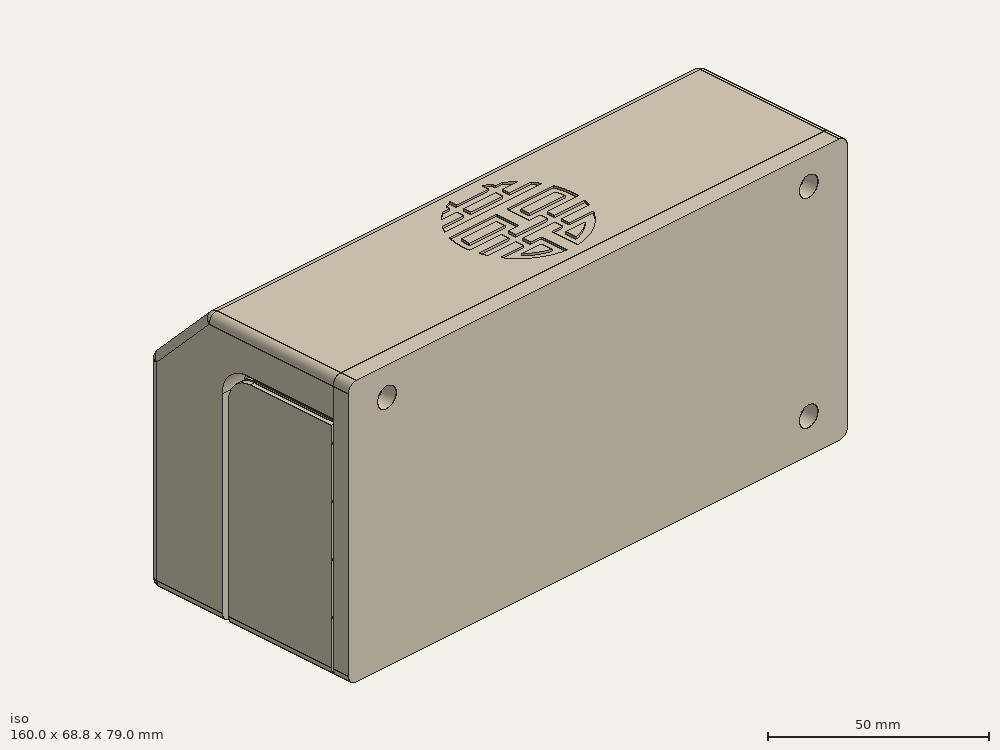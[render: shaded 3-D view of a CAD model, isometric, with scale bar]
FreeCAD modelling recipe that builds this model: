
FCSTD DOCUMENT  (FreeCAD 1.0R39109 (Git))
Label: plastic-player-3
License: All rights reserved
LicenseURL: https://en.wikipedia.org/wiki/All_rights_reserved
objects: Part::Feature×120, Part::Box×46, Part::Mirroring×22, Part::Cylinder×20, Part::MultiFuse×17, Part::Cut×15, App::Part×11, Part::Fillet×11, Part::Chamfer×9, Part::Extrusion×5, Part::Part2DObjectPython×4, Part::FeaturePython×2, Mesh::Feature×2, Sketcher::SketchObject×1
note: 272 computed .brp shape members not serialized (recipe doc carries the construction recipe); baked Part::Feature solids carry a one-line shape summary decoded from their .brp

FEATURE [Part::Box] Box002  label="Cube002"
  AttacherType = Attacher::AttachEngine3D
  Height = 66
  Length = 7
  Placement = pos=(-80,-24.1,-37.5) rot=(0,0,1;0rad)
  Width = 33.6
FEATURE [Part::Cylinder] Cylinder
  Angle = 360
  AttacherType = Attacher::AttachEngine3D
  FirstAngle = 0
  Height = 10
  Placement = pos=(-55,25.5,-3) rot=(-1,0,0;1.5708rad)
  Radius = 12
  SecondAngle = 0
FEATURE [Part::Mirroring] Part__Mirroring001  label="Cylinder (Mirror #2)"
  Base = (0,0,0)
  Normal = (1,0,0)
  Source = -> Cylinder
FEATURE [Part::Cylinder] Cylinder001
  Angle = 360
  AttacherType = Attacher::AttachEngine3D
  FirstAngle = 0
  Height = 10
  Placement = pos=(0,25.5,-15.7) rot=(-1,0,0;1.5708rad)
  Radius = 2.5
  SecondAngle = 0
FEATURE [Part::Box] Box004  label="SlideHolder"
  AttacherType = Attacher::AttachEngine3D
  Height = 25
  Length = 64
  Placement = pos=(-32,34.3405,-9.84497) rot=(1,0,0;0.872665rad)
  Width = 9
FEATURE [Part::Box] Box005  label="Slit"
  AttacherType = Attacher::AttachEngine3D
  Height = 25
  Length = 63
  Placement = pos=(-31.5,39.3167,-9.43399) rot=(1,0,0;0.872665rad)
  Width = 4
FEATURE [Part::Box] Box006  label="Cube003"
  AttacherType = Attacher::AttachEngine3D
  Height = 60
  Length = 150
  Placement = pos=(-75,35,-37.5) rot=(0,0,1;0rad)
  Width = 50
FEATURE [Part::Cylinder] Cylinder002
  Angle = 360
  AttacherType = Attacher::AttachEngine3D
  FirstAngle = 0
  Height = 10
  Placement = pos=(13.9,22.5265,-9.10218) rot=(-1,0,0;0.698132rad)
  Radius = 1.35
  SecondAngle = 0
FEATURE [Part::Cut] Cut003  label="SlideHolderWithScrewHole"
  Base = -> Box004
  Tool = -> Cylinder002
FEATURE [Part::Cut] Cut002  label="SlideHolderCut"
  Base = -> Cut003
  Tool = -> Box006
FEATURE [Part::Box] Box009  label="Window"
  AttacherType = Attacher::AttachEngine3D
  Height = 12.8
  Length = 23.5
  Placement = pos=(-11.8,23.3449,20.5797) rot=(1,0,0;0.785398rad)
  Width = 20
FEATURE [Part::Cylinder] Cylinder005
  Angle = 360
  AttacherType = Attacher::AttachEngine3D
  FirstAngle = 0
  Height = 10
  Placement = pos=(-23.4,25.8452,-12.1479) rot=(-1,0,0;0.698132rad)
  Radius = 1.35
  SecondAngle = 0
FEATURE [Part::Cut] Cut010  label="SlideHolderWithScrewHoles"
  Base = -> Cut002
  Tool = -> Cylinder005
FEATURE [Part::Box] Box010  label="WindowEthernet"
  AttacherType = Attacher::AttachEngine3D
  Height = 16.9
  Length = 10
  Placement = pos=(-81.7,-17.4,3) rot=(0,0,1;0rad)
  Width = 14.7
FEATURE [Part::Box] Box011  label="WindowUSB3"
  AttacherType = Attacher::AttachEngine3D
  Height = 15
  Length = 10
  Placement = pos=(-81.7,-16.6,-14.6) rot=(0,0,1;0rad)
  Width = 15.4
FEATURE [Part::Box] Box012  label="WindowUSB2"
  AttacherType = Attacher::AttachEngine3D
  Height = 15
  Length = 10
  Placement = pos=(-81.7,-16.6,-32.6) rot=(0,0,1;0rad)
  Width = 15.4
FEATURE [Part::Box] Box013  label="Cube006"
  AttacherType = Attacher::AttachEngine3D
  Height = 10
  Length = 12
  Placement = pos=(-6.6,-18.3,-45.9) rot=(0,0,1;0rad)
  Width = 6.2
FEATURE [Part::Cylinder] Cylinder006  label="WindowJackLarge"
  Angle = 360
  AttacherType = Attacher::AttachEngine3D
  FirstAngle = 0
  Height = 10
  Placement = pos=(-43.3,-13.8,-45.8) rot=(0,0,1;0rad)
  Radius = 5
  SecondAngle = 0
FEATURE [Part::Box] Box014  label="Cube007"
  AttacherType = Attacher::AttachEngine3D
  Height = 10
  Length = 27
  Placement = pos=(-35.7,-20.3,-45.9) rot=(0,0,1;0rad)
  Width = 10.5
FEATURE [Part::Box] Box018  label="Cube008"
  AttacherType = Attacher::AttachEngine3D
  Height = 3
  Length = 10
  Placement = pos=(-35.6,27.9576,-4.6521) rot=(-1,0,0;0.698132rad)
  Width = 5
FEATURE [Part::Cut] Cut019  label="SlideHolderWithInsets"
  Base = -> Cut010
  Tool = -> Box018
FEATURE [Part::Box] Box019  label="WindowHDMI1"
  AttacherType = Attacher::AttachEngine3D
  Height = 10
  Length = 9
  Placement = pos=(-19.7,-17.3,-42) rot=(0,0,1;0rad)
  Width = 5
FEATURE [Part::Box] Box020  label="WindowHDMI2"
  AttacherType = Attacher::AttachEngine3D
  Height = 10
  Length = 9
  Placement = pos=(-33.7,-17.3,-42) rot=(0,0,1;0rad)
  Width = 5
FEATURE [Part::Feature] Part__Feature071  label="PCB, RPi4ModelB"
  shape: bbox 85 x 1.6 x 56 mm, 136 faces (baked)
FEATURE [Part::Feature] Part__Feature072  label="Broadcom BCM2711B0 CPU, RPi4ModelB"
  Placement = pos=(-13.25,0.8,-4.5) rot=(0,0,1;0rad)
  shape: bbox 15 x 0.5 x 15 mm, 10 faces (baked)
FEATURE [Part::Feature] Part__Feature073  label="Broadcom BCM2711B0 CPU, RPi4ModelB001"
  Placement = pos=(-13.25,0.8,-4.5) rot=(0,0,1;0rad)
  shape: bbox 14.6 x 1.8 x 14.6 mm, 19 faces (baked)
FEATURE [App::Part] Broadcom_BCM2711B0_CPU__RPi4ModelB  label="Broadcom BCM2711B0 CPU, RPi4ModelB002"
  Group = -> [Part__Feature072,Part__Feature073]
  Origin = -> Origin021
FEATURE [Part::Feature] Part__Feature074  label="2.54 mm DUPONT MALE PIN HEADER, POE, 2X2, RPi4ModelB"
  Placement = pos=(19,0.8,-18.36) rot=(0,0,1;0rad)
  shape: bbox 5.08 x 2.5 x 5.08 mm, 46 faces (baked)
FEATURE [Part::Feature] Part__Feature075  label="2.54 mm DUPONT MALE PIN HEADER, POE, 2X2, RPi4ModelB001"
  Placement = pos=(19,0.8,-18.36) rot=(0,0,1;0rad)
  shape: bbox 0.64 x 11.3 x 0.64 mm, 14 faces (baked)
FEATURE [Part::Feature] Part__Feature076  label="2.54 mm DUPONT MALE PIN HEADER, POE, 2X2, RPi4ModelB002"
  Placement = pos=(19,0.8,-18.36) rot=(0,0,1;0rad)
  shape: bbox 0.64 x 11.3 x 0.64 mm, 14 faces (baked)
FEATURE [Part::Feature] Part__Feature077  label="2.54 mm DUPONT MALE PIN HEADER, POE, 2X2, RPi4ModelB003"
  Placement = pos=(19,0.8,-18.36) rot=(0,0,1;0rad)
  shape: bbox 0.64 x 11.3 x 0.64 mm, 14 faces (baked)
FEATURE [Part::Feature] Part__Feature078  label="2.54 mm DUPONT MALE PIN HEADER, POE, 2X2, RPi4ModelB004"
  Placement = pos=(19,0.8,-18.36) rot=(0,0,1;0rad)
  shape: bbox 0.64 x 11.3 x 0.64 mm, 14 faces (baked)
FEATURE [App::Part] __54_mm_DUPONT_MALE_PIN_HEADER__POE__2X2__RPi4ModelB  label="2.54 mm DUPONT MALE PIN HEADER, POE, 2X2, RPi4ModelB005"
  Group = -> [Part__Feature074,Part__Feature075,Part__Feature076,Part__Feature077,Part__Feature078]
  Origin = -> Origin022
FEATURE [Part::Feature] Part__Feature079  label="2.54 mm DUPONT MALE PIN HEADER, IO, 2X20, RPi4ModelB"
  Placement = pos=(-10,0.8,-24.5) rot=(0,0,1;0rad)
  shape: bbox 50.8 x 2.5 x 5.08 mm, 298 faces (baked)
FEATURE [Part::Feature] Part__Feature080  label="2.54 mm DUPONT MALE PIN HEADER, IO, 2X20, RPi4ModelB001"
  Placement = pos=(-10,0.8,-24.5) rot=(0,0,1;0rad)
  shape: bbox 0.64 x 11.3 x 0.64 mm, 14 faces (baked)
FEATURE [Part::Feature] Part__Feature081  label="2.54 mm DUPONT MALE PIN HEADER, IO, 2X20, RPi4ModelB002"
  Placement = pos=(-10,0.8,-24.5) rot=(0,0,1;0rad)
  shape: bbox 0.64 x 11.3 x 0.64 mm, 14 faces (baked)
FEATURE [Part::Feature] Part__Feature082  label="2.54 mm DUPONT MALE PIN HEADER, IO, 2X20, RPi4ModelB003"
  Placement = pos=(-10,0.8,-24.5) rot=(0,0,1;0rad)
  shape: bbox 0.64 x 11.3 x 0.64 mm, 14 faces (baked)
FEATURE [Part::Feature] Part__Feature083  label="2.54 mm DUPONT MALE PIN HEADER, IO, 2X20, RPi4ModelB004"
  Placement = pos=(-10,0.8,-24.5) rot=(0,0,1;0rad)
  shape: bbox 0.64 x 11.3 x 0.64 mm, 14 faces (baked)
FEATURE [Part::Feature] Part__Feature084  label="2.54 mm DUPONT MALE PIN HEADER, IO, 2X20, RPi4ModelB005"
  Placement = pos=(-10,0.8,-24.5) rot=(0,0,1;0rad)
  shape: bbox 0.64 x 11.3 x 0.64 mm, 14 faces (baked)
FEATURE [Part::Feature] Part__Feature085  label="2.54 mm DUPONT MALE PIN HEADER, IO, 2X20, RPi4ModelB006"
  Placement = pos=(-10,0.8,-24.5) rot=(0,0,1;0rad)
  shape: bbox 0.64 x 11.3 x 0.64 mm, 14 faces (baked)
FEATURE [Part::Feature] Part__Feature086  label="2.54 mm DUPONT MALE PIN HEADER, IO, 2X20, RPi4ModelB007"
  Placement = pos=(-10,0.8,-24.5) rot=(0,0,1;0rad)
  shape: bbox 0.64 x 11.3 x 0.64 mm, 14 faces (baked)
FEATURE [Part::Feature] Part__Feature087  label="2.54 mm DUPONT MALE PIN HEADER, IO, 2X20, RPi4ModelB008"
  Placement = pos=(-10,0.8,-24.5) rot=(0,0,1;0rad)
  shape: bbox 0.64 x 11.3 x 0.64 mm, 14 faces (baked)
FEATURE [Part::Feature] Part__Feature088  label="2.54 mm DUPONT MALE PIN HEADER, IO, 2X20, RPi4ModelB009"
  Placement = pos=(-10,0.8,-24.5) rot=(0,0,1;0rad)
  shape: bbox 0.64 x 11.3 x 0.64 mm, 14 faces (baked)
FEATURE [Part::Feature] Part__Feature089  label="2.54 mm DUPONT MALE PIN HEADER, IO, 2X20, RPi4ModelB010"
  Placement = pos=(-10,0.8,-24.5) rot=(0,0,1;0rad)
  shape: bbox 0.64 x 11.3 x 0.64 mm, 14 faces (baked)
FEATURE [Part::Feature] Part__Feature090  label="2.54 mm DUPONT MALE PIN HEADER, IO, 2X20, RPi4ModelB011"
  Placement = pos=(-10,0.8,-24.5) rot=(0,0,1;0rad)
  shape: bbox 0.64 x 11.3 x 0.64 mm, 14 faces (baked)
FEATURE [Part::Feature] Part__Feature091  label="2.54 mm DUPONT MALE PIN HEADER, IO, 2X20, RPi4ModelB012"
  Placement = pos=(-10,0.8,-24.5) rot=(0,0,1;0rad)
  shape: bbox 0.64 x 11.3 x 0.64 mm, 14 faces (baked)
FEATURE [Part::Feature] Part__Feature092  label="2.54 mm DUPONT MALE PIN HEADER, IO, 2X20, RPi4ModelB013"
  Placement = pos=(-10,0.8,-24.5) rot=(0,0,1;0rad)
  shape: bbox 0.64 x 11.3 x 0.64 mm, 14 faces (baked)
FEATURE [Part::Feature] Part__Feature093  label="2.54 mm DUPONT MALE PIN HEADER, IO, 2X20, RPi4ModelB014"
  Placement = pos=(-10,0.8,-24.5) rot=(0,0,1;0rad)
  shape: bbox 0.64 x 11.3 x 0.64 mm, 14 faces (baked)
FEATURE [Part::Feature] Part__Feature094  label="2.54 mm DUPONT MALE PIN HEADER, IO, 2X20, RPi4ModelB015"
  Placement = pos=(-10,0.8,-24.5) rot=(0,0,1;0rad)
  shape: bbox 0.64 x 11.3 x 0.64 mm, 14 faces (baked)
FEATURE [Part::Feature] Part__Feature095  label="2.54 mm DUPONT MALE PIN HEADER, IO, 2X20, RPi4ModelB016"
  Placement = pos=(-10,0.8,-24.5) rot=(0,0,1;0rad)
  shape: bbox 0.64 x 11.3 x 0.64 mm, 14 faces (baked)
FEATURE [Part::Feature] Part__Feature096  label="2.54 mm DUPONT MALE PIN HEADER, IO, 2X20, RPi4ModelB017"
  Placement = pos=(-10,0.8,-24.5) rot=(0,0,1;0rad)
  shape: bbox 0.64 x 11.3 x 0.64 mm, 14 faces (baked)
FEATURE [Part::Feature] Part__Feature097  label="2.54 mm DUPONT MALE PIN HEADER, IO, 2X20, RPi4ModelB018"
  Placement = pos=(-10,0.8,-24.5) rot=(0,0,1;0rad)
  shape: bbox 0.64 x 11.3 x 0.64 mm, 14 faces (baked)
FEATURE [Part::Feature] Part__Feature098  label="2.54 mm DUPONT MALE PIN HEADER, IO, 2X20, RPi4ModelB019"
  Placement = pos=(-10,0.8,-24.5) rot=(0,0,1;0rad)
  shape: bbox 0.64 x 11.3 x 0.64 mm, 14 faces (baked)
FEATURE [Part::Feature] Part__Feature099  label="2.54 mm DUPONT MALE PIN HEADER, IO, 2X20, RPi4ModelB020"
  Placement = pos=(-10,0.8,-24.5) rot=(0,0,1;0rad)
  shape: bbox 0.64 x 11.3 x 0.64 mm, 14 faces (baked)
FEATURE [Part::Feature] Part__Feature100  label="2.54 mm DUPONT MALE PIN HEADER, IO, 2X20, RPi4ModelB021"
  Placement = pos=(-10,0.8,-24.5) rot=(0,0,1;0rad)
  shape: bbox 0.64 x 11.3 x 0.64 mm, 14 faces (baked)
FEATURE [Part::Feature] Part__Feature101  label="2.54 mm DUPONT MALE PIN HEADER, IO, 2X20, RPi4ModelB022"
  Placement = pos=(-10,0.8,-24.5) rot=(0,0,1;0rad)
  shape: bbox 0.64 x 11.3 x 0.64 mm, 14 faces (baked)
FEATURE [Part::Feature] Part__Feature102  label="2.54 mm DUPONT MALE PIN HEADER, IO, 2X20, RPi4ModelB023"
  Placement = pos=(-10,0.8,-24.5) rot=(0,0,1;0rad)
  shape: bbox 0.64 x 11.3 x 0.64 mm, 14 faces (baked)
FEATURE [Part::Feature] Part__Feature103  label="2.54 mm DUPONT MALE PIN HEADER, IO, 2X20, RPi4ModelB024"
  Placement = pos=(-10,0.8,-24.5) rot=(0,0,1;0rad)
  shape: bbox 0.64 x 11.3 x 0.64 mm, 14 faces (baked)
FEATURE [Part::Feature] Part__Feature104  label="2.54 mm DUPONT MALE PIN HEADER, IO, 2X20, RPi4ModelB025"
  Placement = pos=(-10,0.8,-24.5) rot=(0,0,1;0rad)
  shape: bbox 0.64 x 11.3 x 0.64 mm, 14 faces (baked)
FEATURE [Part::Feature] Part__Feature105  label="2.54 mm DUPONT MALE PIN HEADER, IO, 2X20, RPi4ModelB026"
  Placement = pos=(-10,0.8,-24.5) rot=(0,0,1;0rad)
  shape: bbox 0.64 x 11.3 x 0.64 mm, 14 faces (baked)
FEATURE [Part::Feature] Part__Feature106  label="2.54 mm DUPONT MALE PIN HEADER, IO, 2X20, RPi4ModelB027"
  Placement = pos=(-10,0.8,-24.5) rot=(0,0,1;0rad)
  shape: bbox 0.64 x 11.3 x 0.64 mm, 14 faces (baked)
FEATURE [Part::Feature] Part__Feature107  label="2.54 mm DUPONT MALE PIN HEADER, IO, 2X20, RPi4ModelB028"
  Placement = pos=(-10,0.8,-24.5) rot=(0,0,1;0rad)
  shape: bbox 0.64 x 11.3 x 0.64 mm, 14 faces (baked)
FEATURE [Part::Feature] Part__Feature108  label="2.54 mm DUPONT MALE PIN HEADER, IO, 2X20, RPi4ModelB029"
  Placement = pos=(-10,0.8,-24.5) rot=(0,0,1;0rad)
  shape: bbox 0.64 x 11.3 x 0.64 mm, 14 faces (baked)
FEATURE [Part::Feature] Part__Feature109  label="2.54 mm DUPONT MALE PIN HEADER, IO, 2X20, RPi4ModelB030"
  Placement = pos=(-10,0.8,-24.5) rot=(0,0,1;0rad)
  shape: bbox 0.64 x 11.3 x 0.64 mm, 14 faces (baked)
FEATURE [Part::Feature] Part__Feature110  label="2.54 mm DUPONT MALE PIN HEADER, IO, 2X20, RPi4ModelB031"
  Placement = pos=(-10,0.8,-24.5) rot=(0,0,1;0rad)
  shape: bbox 0.64 x 11.3 x 0.64 mm, 14 faces (baked)
FEATURE [Part::Feature] Part__Feature111  label="2.54 mm DUPONT MALE PIN HEADER, IO, 2X20, RPi4ModelB032"
  Placement = pos=(-10,0.8,-24.5) rot=(0,0,1;0rad)
  shape: bbox 0.64 x 11.3 x 0.64 mm, 14 faces (baked)
FEATURE [Part::Feature] Part__Feature112  label="2.54 mm DUPONT MALE PIN HEADER, IO, 2X20, RPi4ModelB033"
  Placement = pos=(-10,0.8,-24.5) rot=(0,0,1;0rad)
  shape: bbox 0.64 x 11.3 x 0.64 mm, 14 faces (baked)
FEATURE [Part::Feature] Part__Feature113  label="2.54 mm DUPONT MALE PIN HEADER, IO, 2X20, RPi4ModelB034"
  Placement = pos=(-10,0.8,-24.5) rot=(0,0,1;0rad)
  shape: bbox 0.64 x 11.3 x 0.64 mm, 14 faces (baked)
FEATURE [Part::Feature] Part__Feature114  label="2.54 mm DUPONT MALE PIN HEADER, IO, 2X20, RPi4ModelB035"
  Placement = pos=(-10,0.8,-24.5) rot=(0,0,1;0rad)
  shape: bbox 0.64 x 11.3 x 0.64 mm, 14 faces (baked)
FEATURE [Part::Feature] Part__Feature115  label="2.54 mm DUPONT MALE PIN HEADER, IO, 2X20, RPi4ModelB036"
  Placement = pos=(-10,0.8,-24.5) rot=(0,0,1;0rad)
  shape: bbox 0.64 x 11.3 x 0.64 mm, 14 faces (baked)
FEATURE [Part::Feature] Part__Feature116  label="2.54 mm DUPONT MALE PIN HEADER, IO, 2X20, RPi4ModelB037"
  Placement = pos=(-10,0.8,-24.5) rot=(0,0,1;0rad)
  shape: bbox 0.64 x 11.3 x 0.64 mm, 14 faces (baked)
FEATURE [Part::Feature] Part__Feature117  label="2.54 mm DUPONT MALE PIN HEADER, IO, 2X20, RPi4ModelB038"
  Placement = pos=(-10,0.8,-24.5) rot=(0,0,1;0rad)
  shape: bbox 0.64 x 11.3 x 0.64 mm, 14 faces (baked)
FEATURE [Part::Feature] Part__Feature118  label="2.54 mm DUPONT MALE PIN HEADER, IO, 2X20, RPi4ModelB039"
  Placement = pos=(-10,0.8,-24.5) rot=(0,0,1;0rad)
  shape: bbox 0.64 x 11.3 x 0.64 mm, 14 faces (baked)
FEATURE [Part::Feature] Part__Feature119  label="2.54 mm DUPONT MALE PIN HEADER, IO, 2X20, RPi4ModelB040"
  Placement = pos=(-10,0.8,-24.5) rot=(0,0,1;0rad)
  shape: bbox 0.64 x 11.3 x 0.64 mm, 14 faces (baked)
FEATURE [App::Part] __54_mm_DUPONT_MALE_PIN_HEADER__IO__2X20__RPi4ModelB  label="2.54 mm DUPONT MALE PIN HEADER, IO, 2X20, RPi4ModelB041"
  Group = -> [Part__Feature079,Part__Feature080,Part__Feature081,Part__Feature082,Part__Feature083,Part__Feature084,Part__Feature085,Part__Feature086,Part__Feature087,Part__Feature088,Part__Feature089,Part__Feature090,Part__Feature091,Part__Feature092,Part__Feature093,Part__Feature094,Part__Feature095,Part__Feature096,Part__Feature097,Part__Feature098,Part__Feature099,Part__Feature100,Part__Feature101,+18 more]
  Origin = -> Origin023
FEATURE [Part::Feature] Part__Feature120  label="Camera Connector, RPi4ModelB"
  Placement = pos=(4,0.8,16.5) rot=(0,1,0;1.5708rad)
  shape: bbox 4.822 x 4.688 x 0.25 mm, 37 faces (baked)
FEATURE [Part::Feature] Part__Feature121  label="Camera Connector, RPi4ModelB001"
  Placement = pos=(4,0.8,16.5) rot=(0,1,0;1.5708rad)
  shape: bbox 4.822 x 4.688 x 0.25 mm, 37 faces (baked)
FEATURE [Part::Feature] Part__Feature122  label="Camera Connector, RPi4ModelB002"
  Placement = pos=(4,0.8,16.5) rot=(0,1,0;1.5708rad)
  shape: bbox 4.822 x 4.688 x 0.25 mm, 38 faces (baked)
FEATURE [Part::Feature] Part__Feature123  label="Camera Connector, RPi4ModelB003"
  Placement = pos=(4,0.8,16.5) rot=(0,1,0;1.5708rad)
  shape: bbox 4.822 x 4.688 x 0.25 mm, 37 faces (baked)
FEATURE [Part::Feature] Part__Feature124  label="Camera Connector, RPi4ModelB004"
  Placement = pos=(4,0.8,16.5) rot=(0,1,0;1.5708rad)
  shape: bbox 4.822 x 4.688 x 0.25 mm, 37 faces (baked)
FEATURE [Part::Feature] Part__Feature125  label="Camera Connector, RPi4ModelB005"
  Placement = pos=(4,0.8,16.5) rot=(0,1,0;1.5708rad)
  shape: bbox 4.822 x 4.688 x 0.25 mm, 37 faces (baked)
FEATURE [Part::Feature] Part__Feature126  label="Camera Connector, RPi4ModelB006"
  Placement = pos=(4,0.8,16.5) rot=(0,1,0;1.5708rad)
  shape: bbox 4.822 x 4.688 x 0.25 mm, 37 faces (baked)
FEATURE [Part::Feature] Part__Feature127  label="Camera Connector, RPi4ModelB007"
  Placement = pos=(4,0.8,16.5) rot=(0,1,0;1.5708rad)
  shape: bbox 4.822 x 4.688 x 0.25 mm, 37 faces (baked)
FEATURE [Part::Feature] Part__Feature128  label="Camera Connector, RPi4ModelB008"
  Placement = pos=(4,0.8,16.5) rot=(0,1,0;1.5708rad)
  shape: bbox 4.822 x 4.688 x 0.25 mm, 36 faces (baked)
FEATURE [Part::Feature] Part__Feature129  label="Camera Connector, RPi4ModelB009"
  Placement = pos=(4,0.8,16.5) rot=(0,1,0;1.5708rad)
  shape: bbox 4.822 x 4.688 x 0.25 mm, 38 faces (baked)
FEATURE [Part::Feature] Part__Feature130  label="Camera Connector, RPi4ModelB010"
  Placement = pos=(4,0.8,16.5) rot=(0,1,0;1.5708rad)
  shape: bbox 4.822 x 4.688 x 0.25 mm, 37 faces (baked)
FEATURE [Part::Feature] Part__Feature131  label="Camera Connector, RPi4ModelB011"
  Placement = pos=(4,0.8,16.5) rot=(0,1,0;1.5708rad)
  shape: bbox 4.822 x 4.688 x 0.25 mm, 38 faces (baked)
FEATURE [Part::Feature] Part__Feature132  label="Camera Connector, RPi4ModelB012"
  Placement = pos=(4,0.8,16.5) rot=(0,1,0;1.5708rad)
  shape: bbox 4.822 x 4.688 x 0.25 mm, 37 faces (baked)
FEATURE [Part::Feature] Part__Feature133  label="Camera Connector, RPi4ModelB013"
  Placement = pos=(4,0.8,16.5) rot=(0,1,0;1.5708rad)
  shape: bbox 4.822 x 4.688 x 0.25 mm, 37 faces (baked)
FEATURE [Part::Feature] Part__Feature134  label="Camera Connector, RPi4ModelB014"
  Placement = pos=(4,0.8,16.5) rot=(0,1,0;1.5708rad)
  shape: bbox 4.822 x 4.688 x 0.25 mm, 37 faces (baked)
FEATURE [Part::Feature] Part__Feature135  label="Camera Connector, RPi4ModelB015"
  Placement = pos=(4,0.8,16.5) rot=(0,1,0;1.5708rad)
  shape: bbox 3 x 5.3 x 20.6 mm, 382 faces (baked)
FEATURE [Part::Feature] Part__Feature136  label="Camera Connector, RPi4ModelB016"
  Placement = pos=(4,0.8,16.5) rot=(0,1,0;1.5708rad)
  shape: bbox 3.9 x 5.18 x 22.4 mm, 56 faces (baked)
FEATURE [App::Part] Camera_Connector__RPi4ModelB  label="Camera Connector, RPi4ModelB017"
  Group = -> [Part__Feature120,Part__Feature121,Part__Feature122,Part__Feature123,Part__Feature124,Part__Feature125,Part__Feature126,Part__Feature127,Part__Feature128,Part__Feature129,Part__Feature130,Part__Feature131,Part__Feature132,Part__Feature133,Part__Feature134,Part__Feature135,Part__Feature136]
  Origin = -> Origin024
FEATURE [Part::Feature] Part__Feature137  label="Microphone Plug, RPi4ModelB"
  Placement = pos=(11.5,0.8,21.65) rot=(0,0,1;0rad)
  shape: bbox 7.228 x 7.204 x 9.234 mm, 62 faces (baked)
FEATURE [Part::Feature] Part__Feature138  label="Microphone Plug, RPi4ModelB001"
  Placement = pos=(11.5,0.8,21.65) rot=(0,0,1;0rad)
  shape: bbox 2.424 x 7.3 x 8.225 mm, 49 faces (baked)
FEATURE [Part::Feature] Part__Feature139  label="Microphone Plug, RPi4ModelB002"
  Placement = pos=(11.5,0.8,21.65) rot=(0,0,1;0rad)
  shape: bbox 2.388 x 7.3 x 9.047 mm, 49 faces (baked)
FEATURE [Part::Feature] Part__Feature140  label="Microphone Plug, RPi4ModelB003"
  Placement = pos=(11.5,0.8,21.65) rot=(0,0,1;0rad)
  shape: bbox 7 x 7.047 x 15 mm, 115 faces (baked)
FEATURE [Part::Feature] Part__Feature141  label="Microphone Plug, RPi4ModelB004"
  Placement = pos=(11.5,0.8,21.65) rot=(0,0,1;0rad)
  shape: bbox 3.2 x 4.003 x 10.71 mm, 48 faces (baked)
FEATURE [App::Part] Microphone_Plug__RPi4ModelB  label="Microphone Plug, RPi4ModelB005"
  Group = -> [Part__Feature137,Part__Feature138,Part__Feature139,Part__Feature140,Part__Feature141]
  Origin = -> Origin025
FEATURE [Part::Feature] Part__Feature142  label="Display Connector, RPi4ModelB"
  Placement = pos=(-38.5,0.8,0) rot=(0,-1,0;1.5708rad)
  shape: bbox 4.822 x 4.688 x 0.25 mm, 37 faces (baked)
FEATURE [Part::Feature] Part__Feature143  label="Display Connector, RPi4ModelB001"
  Placement = pos=(-38.5,0.8,0) rot=(0,-1,0;1.5708rad)
  shape: bbox 4.822 x 4.688 x 0.25 mm, 37 faces (baked)
FEATURE [Part::Feature] Part__Feature144  label="Display Connector, RPi4ModelB002"
  Placement = pos=(-38.5,0.8,0) rot=(0,-1,0;1.5708rad)
  shape: bbox 4.822 x 4.688 x 0.25 mm, 38 faces (baked)
FEATURE [Part::Feature] Part__Feature145  label="Display Connector, RPi4ModelB003"
  Placement = pos=(-38.5,0.8,0) rot=(0,-1,0;1.5708rad)
  shape: bbox 4.822 x 4.688 x 0.25 mm, 37 faces (baked)
FEATURE [Part::Feature] Part__Feature146  label="Display Connector, RPi4ModelB004"
  Placement = pos=(-38.5,0.8,0) rot=(0,-1,0;1.5708rad)
  shape: bbox 4.822 x 4.688 x 0.25 mm, 37 faces (baked)
FEATURE [Part::Feature] Part__Feature147  label="Display Connector, RPi4ModelB005"
  Placement = pos=(-38.5,0.8,0) rot=(0,-1,0;1.5708rad)
  shape: bbox 4.822 x 4.688 x 0.25 mm, 37 faces (baked)
FEATURE [Part::Feature] Part__Feature148  label="Display Connector, RPi4ModelB006"
  Placement = pos=(-38.5,0.8,0) rot=(0,-1,0;1.5708rad)
  shape: bbox 4.822 x 4.688 x 0.25 mm, 37 faces (baked)
FEATURE [Part::Feature] Part__Feature149  label="Display Connector, RPi4ModelB007"
  Placement = pos=(-38.5,0.8,0) rot=(0,-1,0;1.5708rad)
  shape: bbox 4.822 x 4.688 x 0.25 mm, 37 faces (baked)
FEATURE [Part::Feature] Part__Feature150  label="Display Connector, RPi4ModelB008"
  Placement = pos=(-38.5,0.8,0) rot=(0,-1,0;1.5708rad)
  shape: bbox 4.822 x 4.688 x 0.25 mm, 36 faces (baked)
FEATURE [Part::Feature] Part__Feature151  label="Display Connector, RPi4ModelB009"
  Placement = pos=(-38.5,0.8,0) rot=(0,-1,0;1.5708rad)
  shape: bbox 4.822 x 4.688 x 0.25 mm, 38 faces (baked)
FEATURE [Part::Feature] Part__Feature152  label="Display Connector, RPi4ModelB010"
  Placement = pos=(-38.5,0.8,0) rot=(0,-1,0;1.5708rad)
  shape: bbox 4.822 x 4.688 x 0.25 mm, 37 faces (baked)
FEATURE [Part::Feature] Part__Feature153  label="Display Connector, RPi4ModelB011"
  Placement = pos=(-38.5,0.8,0) rot=(0,-1,0;1.5708rad)
  shape: bbox 4.822 x 4.688 x 0.25 mm, 38 faces (baked)
FEATURE [Part::Feature] Part__Feature154  label="Display Connector, RPi4ModelB012"
  Placement = pos=(-38.5,0.8,0) rot=(0,-1,0;1.5708rad)
  shape: bbox 4.822 x 4.688 x 0.25 mm, 37 faces (baked)
FEATURE [Part::Feature] Part__Feature155  label="Display Connector, RPi4ModelB013"
  Placement = pos=(-38.5,0.8,0) rot=(0,-1,0;1.5708rad)
  shape: bbox 4.822 x 4.688 x 0.25 mm, 37 faces (baked)
FEATURE [Part::Feature] Part__Feature156  label="Display Connector, RPi4ModelB014"
  Placement = pos=(-38.5,0.8,0) rot=(0,-1,0;1.5708rad)
  shape: bbox 4.822 x 4.688 x 0.25 mm, 37 faces (baked)
FEATURE [Part::Feature] Part__Feature157  label="Display Connector, RPi4ModelB015"
  Placement = pos=(-38.5,0.8,0) rot=(0,-1,0;1.5708rad)
  shape: bbox 3 x 5.3 x 20.6 mm, 382 faces (baked)
FEATURE [Part::Feature] Part__Feature158  label="Display Connector, RPi4ModelB016"
  Placement = pos=(-38.5,0.8,0) rot=(0,-1,0;1.5708rad)
  shape: bbox 3.9 x 5.18 x 22.4 mm, 56 faces (baked)
FEATURE [App::Part] Display_Connector__RPi4ModelB  label="Display Connector, RPi4ModelB017"
  Group = -> [Part__Feature142,Part__Feature143,Part__Feature144,Part__Feature145,Part__Feature146,Part__Feature147,Part__Feature148,Part__Feature149,Part__Feature150,Part__Feature151,Part__Feature152,Part__Feature153,Part__Feature154,Part__Feature155,Part__Feature156,Part__Feature157,Part__Feature158]
  Origin = -> Origin026
FEATURE [Part::Feature] Part__Feature159  label="Gigabit Ethernet Port, RPi4ModelB"
  Placement = pos=(45.5,7.55,-17.75) rot=(0,1,0;1.5708rad)
  shape: bbox 21.6 x 17.23 x 16.33 mm, 403 faces (baked)
FEATURE [Part::Feature] Part__Feature160  label="Female Micro HDMI Connector, RPi4ModelB"
  Placement = pos=(-3,0.8,27.3875) rot=(0,0,1;0rad)
  shape: bbox 6.501 x 3.516 x 7.501 mm, 1058 faces (baked)
FEATURE [Part::Feature] Part__Feature161  label="Female Micro HDMI Connector, RPi4ModelB001"
  Placement = pos=(-16.5,0.8,27.3875) rot=(0,0,1;0rad)
  shape: bbox 6.501 x 3.516 x 7.501 mm, 1058 faces (baked)
FEATURE [Part::Feature] Part__Feature162  label="Female USB Type C Connector, RPi4ModelB"
  Placement = pos=(-31.3,0.8,26.5419) rot=(0,0,1;0rad)
  shape: bbox 8.94 x 3.96 x 7.9 mm, 403 faces (baked)
FEATURE [Part::Feature] Part__Feature163  label="2X USB3.0 PORTS, RPi4ModelB"
  Placement = pos=(37.07,0.8,1) rot=(0,0,1;0rad)
  shape: bbox 17.47 x 19.41 x 15.83 mm, 1044 faces (baked)
FEATURE [Part::Feature] Part__Feature164  label="91D77 D9WHV 778K, 4 GB LPDDR4 SDRAM, RPi4ModelB"
  Placement = pos=(2.25,0.8,-4.5) rot=(0,0,1;0rad)
  shape: bbox 10 x 0.8 x 14.5 mm, 180 faces (baked)
FEATURE [Part::Feature] Part__Feature165  label="Cypress CYW43455 Wireless Module Cover, RPi4ModelB"
  Placement = pos=(-30.5,0.8,-14.5) rot=(0,0,1;0rad)
  shape: bbox 11 x 1.6 x 13 mm, 70 faces (baked)
FEATURE [Part::Feature] Part__Feature166  label="SD Card Slot, RPi4ModelB"
  Placement = pos=(-35.3,-0.8,-1e-14) rot=(0.707107,0,-0.707107;3.14159rad)
  shape: bbox 11.4 x 1.45 x 11.95 mm, 218 faces (baked)
FEATURE [Part::Feature] Part__Feature167  label="SD Card Slot, RPi4ModelB001"
  Placement = pos=(-35.3,-0.8,-1e-14) rot=(0.707107,0,-0.707107;3.14159rad)
  shape: bbox 7.946 x 0.8923 x 0.34 mm, 23 faces (baked)
FEATURE [Part::Feature] Part__Feature168  label="SD Card Slot, RPi4ModelB002"
  Placement = pos=(-35.3,-0.8,-1e-14) rot=(0.707107,0,-0.707107;3.14159rad)
  shape: bbox 7.946 x 0.8923 x 0.34 mm, 23 faces (baked)
FEATURE [Part::Feature] Part__Feature169  label="SD Card Slot, RPi4ModelB003"
  Placement = pos=(-35.3,-0.8,-1e-14) rot=(0.707107,0,-0.707107;3.14159rad)
  shape: bbox 7.946 x 0.8923 x 0.34 mm, 22 faces (baked)
FEATURE [Part::Feature] Part__Feature170  label="SD Card Slot, RPi4ModelB004"
  Placement = pos=(-35.3,-0.8,-1e-14) rot=(0.707107,0,-0.707107;3.14159rad)
  shape: bbox 7.946 x 0.8923 x 0.34 mm, 23 faces (baked)
FEATURE [Part::Feature] Part__Feature171  label="SD Card Slot, RPi4ModelB005"
  Placement = pos=(-35.3,-0.8,-1e-14) rot=(0.707107,0,-0.707107;3.14159rad)
  shape: bbox 7.946 x 0.8923 x 0.34 mm, 23 faces (baked)
FEATURE [Part::Feature] Part__Feature172  label="SD Card Slot, RPi4ModelB006"
  Placement = pos=(-35.3,-0.8,-1e-14) rot=(0.707107,0,-0.707107;3.14159rad)
  shape: bbox 7.946 x 0.8923 x 0.34 mm, 22 faces (baked)
FEATURE [Part::Feature] Part__Feature173  label="SD Card Slot, RPi4ModelB007"
  Placement = pos=(-35.3,-0.8,-1e-14) rot=(0.707107,0,-0.707107;3.14159rad)
  shape: bbox 7.946 x 0.8923 x 0.34 mm, 23 faces (baked)
FEATURE [Part::Feature] Part__Feature174  label="SD Card Slot, RPi4ModelB008"
  Placement = pos=(-35.3,-0.8,-1e-14) rot=(0.707107,0,-0.707107;3.14159rad)
  shape: bbox 7.946 x 0.8923 x 0.34 mm, 22 faces (baked)
FEATURE [Part::Feature] Part__Feature175  label="SD Card Slot, RPi4ModelB009"
  Placement = pos=(-35.3,-0.8,-1e-14) rot=(0.707107,0,-0.707107;3.14159rad)
  shape: bbox 10.28 x 1.3 x 11.71 mm, 80 faces (baked)
FEATURE [App::Part] SD_Card_Slot__RPi4ModelB  label="SD Card Slot, RPi4ModelB010"
  Group = -> [Part__Feature166,Part__Feature167,Part__Feature168,Part__Feature169,Part__Feature170,Part__Feature171,Part__Feature172,Part__Feature173,Part__Feature174,Part__Feature175]
  Origin = -> Origin027
FEATURE [Part::Feature] Part__Feature176  label="VIA VL805 PCIe USB 3.0 controller, RPi4ModelB"
  Placement = pos=(17.5,0.8,4) rot=(0,0,1;0rad)
  shape: bbox 8.8 x 0.8 x 8.8 mm, 398 faces (baked)
FEATURE [Part::Feature] Part__Feature177  label="2X USB2.0 PORTS, RPi4ModelB"
  Placement = pos=(37.065,0.65,19) rot=(0,0,1;0rad)
  shape: bbox 17.86 x 19.16 x 15.45 mm, 1086 faces (baked)
FEATURE [Part::Feature] Part__Feature178  label="Broadcom BCM54213PE Gigabit Ethernet Transceiver, RPi4ModelB"
  Placement = pos=(16.5,0.8,-10) rot=(0,0,1;0rad)
  shape: bbox 6.802 x 1.002 x 6.802 mm, 559 faces (baked)
FEATURE [Part::Feature] Part__Feature179  label="MxL7704 Universal PMIC, RPi4ModelB"
  Placement = pos=(-32.5,0.8,16) rot=(0,0,1;0rad)
  shape: bbox 5.4 x 0.8 x 5.4 mm, 311 faces (baked)
FEATURE [App::Part] Raspberry_Pi_4_Model_B  label="Raspberry Pi 4 Model B"
  Group = -> [Part__Feature071,Broadcom_BCM2711B0_CPU__RPi4ModelB,__54_mm_DUPONT_MALE_PIN_HEADER__POE__2X2__RPi4ModelB,__54_mm_DUPONT_MALE_PIN_HEADER__IO__2X20__RPi4ModelB,Camera_Connector__RPi4ModelB,Microphone_Plug__RPi4ModelB,Display_Connector__RPi4ModelB,Part__Feature159,Part__Feature160,Part__Feature161,Part__Feature162,Part__Feature163,Part__Feature164,Part__Feature165,SD_Card_Slot__RPi4ModelB,+4 more]
  Origin = -> Origin028
  Placement = pos=(-31.8,-17.8,-6.3) rot=(0,1,0;3.14159rad)
FEATURE [Part::Feature] Part__Feature180  label="RC522"
  Placement = pos=(-9.1,15.9628,2.78316) rot=(0.389282,-0.834817,-0.389282;1.75037rad)
  shape: bbox 65.45 x 32.01 x 26.35 mm, 426 faces (baked)
FEATURE [Part::Box] Box022  label="Cube012"
  AttacherType = Attacher::AttachEngine3D
  Height = 79
  Length = 160
  Placement = pos=(-80,-29,-37.5) rot=(0,0,1;0rad)
  Width = 4.9
FEATURE [Part::Box] Box023  label="Cube013"
  AttacherType = Attacher::AttachEngine3D
  Height = 66.8
  Length = 141.8
  Placement = pos=(-70.9,-29,-30.4) rot=(0,0,1;0rad)
  Width = 6.9
FEATURE [Part::Cylinder] Cylinder007
  Angle = 360
  AttacherType = Attacher::AttachEngine3D
  FirstAngle = 0
  Height = 10
  Placement = pos=(-50.8,-15.4,-30.8) rot=(1,0,0;1.5708rad)
  Radius = 1
  SecondAngle = 0
FEATURE [Part::MultiFuse] Fusion003  label="BottomPlateOld"
  Shapes = -> [Box023,Box022]
FEATURE [Part::Mirroring] Part__Mirroring  label="Cylinder007 (Mirror #4)"
  Base = (-21.8,0,-30.8)
  Normal = (1,-1e-16,-3.57628e-07)
  Source = -> Cylinder007
FEATURE [Part::Mirroring] Part__Mirroring006  label="Cylinder007 (Mirror #5)"
  Base = (0,0,-6.3)
  Normal = (0,0,1)
  Source = -> Cylinder007
FEATURE [Part::Mirroring] Part__Mirroring007  label="Cylinder007 (Mirror #6)"
  Base = (0,0,-6.3)
  Normal = (0,0,1)
  Source = -> Part__Mirroring
FEATURE [Part::MultiFuse] Fusion004  label="RPiScrewHoles"
  Shapes = -> [Cylinder007,Part__Mirroring006,Part__Mirroring007,Part__Mirroring]
FEATURE [Part::FeaturePython] Tube  # WARN: FeaturePython — macro-defined, semantics opaque (R4)
  AttacherType = Attacher::AttachEngine3D
  Height = 3.3
  InnerRadius = 1
  OuterRadius = 3
  Placement = pos=(-50.8,-22.1,-30.8) rot=(-1,0,0;1.5708rad)
FEATURE [Part::Mirroring] Part__Mirroring008  label="Tube (Mirror #7)"
  Base = (-21.8,0,0)
  Normal = (1,0,0)
  Source = -> Tube
FEATURE [Part::Mirroring] Part__Mirroring009  label="Tube (Mirror #8)"
  Base = (0,0,-6.3)
  Normal = (0,0,1)
  Source = -> Tube
FEATURE [Part::Mirroring] Part__Mirroring010  label="Tube (Mirror #9)"
  Base = (0,0,-6.3)
  Normal = (0,0,1)
  Source = -> Part__Mirroring008
FEATURE [Part::Cylinder] Cylinder008
  Angle = 360
  AttacherType = Attacher::AttachEngine3D
  FirstAngle = 0
  Height = 10
  Placement = pos=(67.65,-18,-27.15) rot=(1,0,0;1.5708rad)
  Radius = 1.8
  SecondAngle = 0
FEATURE [Part::Cylinder] Cylinder009
  Angle = 360
  AttacherType = Attacher::AttachEngine3D
  FirstAngle = 0
  Height = 4
  Placement = pos=(67.65,-25,-27.1) rot=(1,0,0;1.5708rad)
  Radius = 3
  SecondAngle = 0
FEATURE [Part::Box] Box028  label="Cube018"
  AttacherType = Attacher::AttachEngine3D
  Height = 7
  Length = 7
  Placement = pos=(71,-22,36.5) rot=(0,1,0;3.14159rad)
  Width = 10
FEATURE [Part::Feature] Part__Feature181  label="Base"
  shape: bbox 29.44 x 29.72 x 21 mm, 79 faces (baked)
FEATURE [Part::Feature] Part__Feature182  label="microswitch v2"
  Placement = pos=(-7e-15,0,-9.176) rot=(0,0,1;0rad)
  shape: bbox 15.01 x 12.07 x 29.85 mm, 136 faces (baked)
FEATURE [Part::Feature] Part__Feature183  label="Top cap"
  shape: bbox 24 x 21.11 x 12.44 mm, 68 faces (baked)
FEATURE [Part::Box] Box029  label="BottomBackWall"
  AttacherType = Attacher::AttachEngine3D
  Height = 5
  Length = 95
  Placement = pos=(-80,-24.1,-37.5) rot=(0,0,1;0rad)
  Width = 33.6
FEATURE [Part::Cylinder] Cylinder010  label="WindowJackSmall"
  Angle = 360
  AttacherType = Attacher::AttachEngine3D
  FirstAngle = 0
  Height = 10
  Placement = pos=(-43.3,-13.8,-42.1) rot=(0,0,1;0rad)
  Radius = 4
  SecondAngle = 0
FEATURE [Part::Box] Box030  label="WindowUSBCSmall"
  AttacherType = Attacher::AttachEngine3D
  Height = 10
  Length = 10
  Placement = pos=(-5.7,-17.3,-42.5) rot=(0,0,1;0rad)
  Width = 4.2
FEATURE [Part::Box] Box032  label="Cube021"
  AttacherType = Attacher::AttachEngine3D
  Height = 10
  Length = 10
  Width = 10
FEATURE [Part::Box] Box033  label="Cube022"
  AttacherType = Attacher::AttachEngine3D
  Height = 10
  Length = 10
  Width = 10
FEATURE [Part::Box] Box034  label="Cube023"
  AttacherType = Attacher::AttachEngine3D
  Height = 10
  Length = 10
  Width = 10
FEATURE [Part::Box] Box035  label="Cube024"
  AttacherType = Attacher::AttachEngine3D
  Height = 10
  Length = 10
  Width = 10
FEATURE [Part::Box] Box036  label="Cube025"
  AttacherType = Attacher::AttachEngine3D
  Height = 10
  Length = 10
  Width = 10
FEATURE [Part::Box] Box037  label="Cube026"
  AttacherType = Attacher::AttachEngine3D
  Height = 10
  Length = 10
  Width = 10
FEATURE [Part::Box] Box038  label="Cube027"
  AttacherType = Attacher::AttachEngine3D
  Height = 10
  Length = 10
  Width = 10
FEATURE [Part::Box] Box039  label="Cube028"
  AttacherType = Attacher::AttachEngine3D
  Height = 10
  Length = 10
  Width = 10
FEATURE [Part::Box] Box040  label="Cube029"
  AttacherType = Attacher::AttachEngine3D
  Height = 10
  Length = 10
  Width = 10
FEATURE [App::Part] Yellow_24mm_button_v5  label="Yellow 24mm button v5"
  Group = -> [Part__Feature181,Part__Feature182,Part__Feature183,Box032,Box033,Box034,Box035,Box036,Box037,Box038,Box039,Box040]
  Origin = -> Origin030
  Placement = pos=(55,20.3,-3) rot=(-1,0,0;1.5708rad)
FEATURE [Part::Mirroring] Part__Mirroring014  label="Yellow 24mm button v5 (Mirror #13)"
  Base = (-2.38419e-07,20.1915,-3)
  Normal = (1,-1e-16,-3.57628e-07)
  Source = -> Yellow_24mm_button_v5
FEATURE [Part::Box] Box042  label="Cube031"
  AttacherType = Attacher::AttachEngine3D
  Height = 5.1
  Length = 97
  Placement = pos=(-80,-24,-37.5) rot=(0,0,1;0rad)
  Width = 35.5
FEATURE [Part::Box] Box044  label="Cube033"
  AttacherType = Attacher::AttachEngine3D
  Height = 61
  Length = 91
  Placement = pos=(-80,-24,-37.5) rot=(0,0,1;0rad)
  Width = 25
FEATURE [Part::Box] Box045  label="Cube034"
  AttacherType = Attacher::AttachEngine3D
  Height = 68
  Length = 7.1
  Placement = pos=(-80,-24,-37.5) rot=(0,0,1;0rad)
  Width = 35.5
FEATURE [Part::Chamfer] Chamfer004
  Base = -> Box028
  EdgeLinks = -> Box028 [Edge7,Edge12]
  Edges = 2 edges r=6.9: [Edge7,Edge12]
FEATURE [Part::Mirroring] Part__Mirroring016  label="Chamfer004 (Mirror #12)"
  Base = (0,0,0)
  Normal = (1,0,0)
  Source = -> Chamfer004
FEATURE [Part::Mirroring] Part__Mirroring017  label="Chamfer004 (Mirror #13)"
  Base = (70.5,-17,3)
  Normal = (0,0,1)
  Source = -> Chamfer004
FEATURE [Part::Feature] Part__Feature196  label="Part2"
  Placement = pos=(9.95684,8.65312,2.616) rot=(-0.707107,0.707107,0;3.14159rad)
  shape: bbox 26.38 x 26.2 x 2.84 mm, 44 faces (baked)
FEATURE [Part::Feature] Part__Feature197  label="brep_2"
  shape: bbox 0.6304 x 0.63 x 11.7 mm, 10 faces (baked)
FEATURE [Part::Feature] Part__Feature198  label="brep_003"
  Placement = pos=(-2.54,0,0) rot=(0,0,1;0rad)
  shape: bbox 0.6304 x 0.63 x 11.7 mm, 10 faces (baked)
FEATURE [Part::Feature] Part__Feature199  label="brep_004"
  Placement = pos=(-5.08,0,0) rot=(0,0,1;0rad)
  shape: bbox 0.6304 x 0.63 x 11.7 mm, 10 faces (baked)
FEATURE [Part::Feature] Part__Feature200  label="brep_005"
  Placement = pos=(-7.62,0,0) rot=(0,0,1;0rad)
  shape: bbox 0.6304 x 0.63 x 11.7 mm, 10 faces (baked)
FEATURE [Part::Feature] Part__Feature201  label="shell_1"
  shape: bbox 10.16 x 2.54 x 2.799 mm, 90 faces (baked)
FEATURE [App::Part] Assembly1
  Group = -> [Part__Feature197,Part__Feature198,Part__Feature199,Part__Feature200,Part__Feature201]
  Origin = -> Origin033
  Placement = pos=(-9.20789,3.78068,2.8) rot=(0,0,-1;1.5708rad)
FEATURE [App::Part] OLED_TEMU_0_96_in  label="OLED TEMU 0.96 in"
  Group = -> [Part__Feature196,Assembly1]
  Origin = -> Origin034
  Placement = pos=(5.9e-15,24.0475,29.0645) rot=(-0.678598,0.678598,-0.281085;3.68962rad)
FEATURE [Part::Cylinder] Cylinder011
  Angle = 360
  AttacherType = Attacher::AttachEngine3D
  FirstAngle = 0
  Height = 10
  Placement = pos=(67.65,-18,-27.1) rot=(1,0,0;1.5708rad)
  Radius = 1.35
  SecondAngle = 0
FEATURE [Part::Mirroring] Part__Mirroring018  label="Cylinder011 (Mirror #14)"
  Base = (0,0,3)
  Normal = (0,0,1)
  Source = -> Cylinder011
FEATURE [Mesh::Feature] plastic_Back_2024_09_17b  label="plastic-Back-2024-09-17b"
  Placement = pos=(0,50.6095,-3.52767) rot=(-1,0,0;0.698132rad)
FEATURE [Mesh::Feature] plastic_Front_2024_09_17b  label="plastic-Front-2024-09-17b"
  Placement = pos=(0,42.8748,-12.5997) rot=(-1,0,0;0.698132rad)
FEATURE [Part::Box] Box  label="SpacerCoverSlider2"
  AttacherType = Attacher::AttachEngine3D
  Height = 62.75
  Length = 1.3
  Placement = pos=(-78.1,-23.1,-37.5) rot=(0,0,1;0rad)
  Width = 29.1
FEATURE [Part::Fillet] Fillet004  label="WindowHDMILarge"
  Base = -> Box014
  EdgeLinks = -> Box014 [Edge1,Edge3,Edge5,Edge7]
  Edges = 4 edges r=2: [Edge1,Edge3,Edge5,Edge7]
FEATURE [Part::Fillet] Fillet005  label="WindowUSBCLarge"
  Base = -> Box013
  EdgeLinks = -> Box013 [Edge1,Edge3,Edge5,Edge7]
  Edges = 4 edges r=2: [Edge1,Edge3,Edge5,Edge7]
FEATURE [Sketcher::SketchObject] Sketch
  ArcFitTolerance = 0
  FullyConstrained = false
  MakeInternals = false
  Placement = pos=(0,0,0) rot=(0,0,1;3.14159rad)
  sketch-geometry (76):
    g0: BSplineCurve PolesCount=2 KnotsCount=2 Degree=1 IsPeriodic=0
    g1: BSplineCurve PolesCount=3 KnotsCount=2 Degree=2 IsPeriodic=0
    g2: BSplineCurve PolesCount=2 KnotsCount=2 Degree=1 IsPeriodic=0
    g3: BSplineCurve PolesCount=2 KnotsCount=2 Degree=1 IsPeriodic=0
    g4: BSplineCurve PolesCount=2 KnotsCount=2 Degree=1 IsPeriodic=0
    g5: BSplineCurve PolesCount=3 KnotsCount=2 Degree=2 IsPeriodic=0
    g6: BSplineCurve PolesCount=2 KnotsCount=2 Degree=1 IsPeriodic=0
    g7: BSplineCurve PolesCount=2 KnotsCount=2 Degree=1 IsPeriodic=0
    g8: BSplineCurve PolesCount=3 KnotsCount=2 Degree=2 IsPeriodic=0
    g9: BSplineCurve PolesCount=2 KnotsCount=2 Degree=1 IsPeriodic=0
    g10: BSplineCurve PolesCount=2 KnotsCount=2 Degree=1 IsPeriodic=0
    g11: BSplineCurve PolesCount=2 KnotsCount=2 Degree=1 IsPeriodic=0
    g12: BSplineCurve PolesCount=3 KnotsCount=2 Degree=2 IsPeriodic=0
    g13: BSplineCurve PolesCount=2 KnotsCount=2 Degree=1 IsPeriodic=0
    g14: BSplineCurve PolesCount=2 KnotsCount=2 Degree=1 IsPeriodic=0
    g15: BSplineCurve PolesCount=3 KnotsCount=2 Degree=2 IsPeriodic=0
    g16: BSplineCurve PolesCount=2 KnotsCount=2 Degree=1 IsPeriodic=0
    g17: BSplineCurve PolesCount=2 KnotsCount=2 Degree=1 IsPeriodic=0
    g18: BSplineCurve PolesCount=2 KnotsCount=2 Degree=1 IsPeriodic=0
    g19: BSplineCurve PolesCount=3 KnotsCount=2 Degree=2 IsPeriodic=0
    g20: BSplineCurve PolesCount=3 KnotsCount=2 Degree=2 IsPeriodic=0
    g21: BSplineCurve PolesCount=2 KnotsCount=2 Degree=1 IsPeriodic=0
    g22: BSplineCurve PolesCount=2 KnotsCount=2 Degree=1 IsPeriodic=0
    g23: BSplineCurve PolesCount=2 KnotsCount=2 Degree=1 IsPeriodic=0
    g24: BSplineCurve PolesCount=3 KnotsCount=2 Degree=2 IsPeriodic=0
    g25: BSplineCurve PolesCount=2 KnotsCount=2 Degree=1 IsPeriodic=0
    g26: BSplineCurve PolesCount=2 KnotsCount=2 Degree=1 IsPeriodic=0
    g27: BSplineCurve PolesCount=2 KnotsCount=2 Degree=1 IsPeriodic=0
    g28: BSplineCurve PolesCount=3 KnotsCount=2 Degree=2 IsPeriodic=0
    g29: BSplineCurve PolesCount=3 KnotsCount=2 Degree=2 IsPeriodic=0
    g30: BSplineCurve PolesCount=2 KnotsCount=2 Degree=1 IsPeriodic=0
    g31: BSplineCurve PolesCount=2 KnotsCount=2 Degree=1 IsPeriodic=0
    g32: BSplineCurve PolesCount=2 KnotsCount=2 Degree=1 IsPeriodic=0
    g33: BSplineCurve PolesCount=2 KnotsCount=2 Degree=1 IsPeriodic=0
    g34: BSplineCurve PolesCount=2 KnotsCount=2 Degree=1 IsPeriodic=0
    g35: BSplineCurve PolesCount=2 KnotsCount=2 Degree=1 IsPeriodic=0
    g36: BSplineCurve PolesCount=2 KnotsCount=2 Degree=1 IsPeriodic=0
    g37: BSplineCurve PolesCount=3 KnotsCount=2 Degree=2 IsPeriodic=0
    g38: BSplineCurve PolesCount=3 KnotsCount=2 Degree=2 IsPeriodic=0
    g39: BSplineCurve PolesCount=2 KnotsCount=2 Degree=1 IsPeriodic=0
    g40: BSplineCurve PolesCount=2 KnotsCount=2 Degree=1 IsPeriodic=0
    g41: BSplineCurve PolesCount=2 KnotsCount=2 Degree=1 IsPeriodic=0
    g42: BSplineCurve PolesCount=3 KnotsCount=2 Degree=2 IsPeriodic=0
    g43: BSplineCurve PolesCount=2 KnotsCount=2 Degree=1 IsPeriodic=0
    g44: BSplineCurve PolesCount=2 KnotsCount=2 Degree=1 IsPeriodic=0
    g45: BSplineCurve PolesCount=2 KnotsCount=2 Degree=1 IsPeriodic=0
    g46: BSplineCurve PolesCount=3 KnotsCount=2 Degree=2 IsPeriodic=0
    g47: BSplineCurve PolesCount=3 KnotsCount=2 Degree=2 IsPeriodic=0
    g48: BSplineCurve PolesCount=2 KnotsCount=2 Degree=1 IsPeriodic=0
    g49: BSplineCurve PolesCount=2 KnotsCount=2 Degree=1 IsPeriodic=0
    g50: BSplineCurve PolesCount=2 KnotsCount=2 Degree=1 IsPeriodic=0
    g51: BSplineCurve PolesCount=2 KnotsCount=2 Degree=1 IsPeriodic=0
    g52: BSplineCurve PolesCount=2 KnotsCount=2 Degree=1 IsPeriodic=0
    g53: BSplineCurve PolesCount=2 KnotsCount=2 Degree=1 IsPeriodic=0
    g54: BSplineCurve PolesCount=2 KnotsCount=2 Degree=1 IsPeriodic=0
    g55: BSplineCurve PolesCount=2 KnotsCount=2 Degree=1 IsPeriodic=0
    g56: BSplineCurve PolesCount=2 KnotsCount=2 Degree=1 IsPeriodic=0
    g57: BSplineCurve PolesCount=3 KnotsCount=2 Degree=2 IsPeriodic=0
    g58: BSplineCurve PolesCount=3 KnotsCount=2 Degree=2 IsPeriodic=0
    g59: BSplineCurve PolesCount=2 KnotsCount=2 Degree=1 IsPeriodic=0
    g60: BSplineCurve PolesCount=2 KnotsCount=2 Degree=1 IsPeriodic=0
    g61: BSplineCurve PolesCount=2 KnotsCount=2 Degree=1 IsPeriodic=0
    g62: BSplineCurve PolesCount=2 KnotsCount=2 Degree=1 IsPeriodic=0
    g63: BSplineCurve PolesCount=2 KnotsCount=2 Degree=1 IsPeriodic=0
    g64: BSplineCurve PolesCount=2 KnotsCount=2 Degree=1 IsPeriodic=0
    g65: BSplineCurve PolesCount=2 KnotsCount=2 Degree=1 IsPeriodic=0
    g66: BSplineCurve PolesCount=2 KnotsCount=2 Degree=1 IsPeriodic=0
    g67: BSplineCurve PolesCount=2 KnotsCount=2 Degree=1 IsPeriodic=0
    g68: BSplineCurve PolesCount=3 KnotsCount=2 Degree=2 IsPeriodic=0
    g69: BSplineCurve PolesCount=2 KnotsCount=2 Degree=1 IsPeriodic=0
    g70: BSplineCurve PolesCount=2 KnotsCount=2 Degree=1 IsPeriodic=0
    g71: BSplineCurve PolesCount=3 KnotsCount=2 Degree=2 IsPeriodic=0
    g72: BSplineCurve PolesCount=2 KnotsCount=2 Degree=1 IsPeriodic=0
    g73: BSplineCurve PolesCount=2 KnotsCount=2 Degree=1 IsPeriodic=0
    g74: BSplineCurve PolesCount=2 KnotsCount=2 Degree=1 IsPeriodic=0
    g75: BSplineCurve PolesCount=3 KnotsCount=2 Degree=2 IsPeriodic=0
  constraints (76):
    c: Coincident(g0,g1)
    c: Coincident(g1,g2)
    c: Coincident(g2,g3)
    c: Coincident(g3,g4)
    c: Coincident(g4,g5)
    c: Coincident(g5,g6)
    c: Coincident(g6,g7)
    c: Coincident(g7,g8)
    c: Coincident(g8,g9)
    c: Coincident(g9,g10)
    c: Coincident(g10,g11)
    c: Coincident(g11,g12)
    c: Coincident(g12,g13)
    c: Coincident(g13,g14)
    c: Coincident(g14,g15)
    c: Coincident(g15,g16)
    c: Coincident(g16,g17)
    c: Coincident(g17,g18)
    c: Coincident(g18,g19)
    c: Coincident(g19,g0)
    c: Coincident(g20,g21)
    c: Coincident(g21,g22)
    c: Coincident(g22,g23)
    c: Coincident(g23,g24)
    c: Coincident(g24,g25)
    c: Coincident(g25,g26)
    c: Coincident(g26,g27)
    c: Coincident(g27,g28)
    c: Coincident(g28,g29)
    c: Coincident(g29,g30)
    c: Coincident(g30,g31)
    c: Coincident(g31,g32)
    c: Coincident(g32,g33)
    c: Coincident(g33,g34)
    c: Coincident(g34,g35)
    c: Coincident(g35,g36)
    c: Coincident(g36,g37)
    c: Coincident(g37,g38)
    c: Coincident(g38,g39)
    c: Coincident(g39,g40)
    c: Coincident(g40,g41)
    c: Coincident(g41,g42)
    c: Coincident(g42,g43)
    c: Coincident(g43,g44)
    c: Coincident(g44,g45)
    c: Coincident(g45,g46)
    c: Coincident(g46,g47)
    c: Coincident(g47,g48)
    c: Coincident(g48,g49)
    c: Coincident(g49,g50)
    c: Coincident(g50,g51)
    c: Coincident(g51,g52)
    c: Coincident(g52,g53)
    c: Coincident(g53,g54)
    c: Coincident(g54,g55)
    c: Coincident(g55,g56)
    c: Coincident(g56,g57)
    c: Coincident(g57,g20)
    c: Coincident(g58,g59)
    c: Coincident(g59,g60)
    c: Coincident(g60,g61)
    c: Coincident(g61,g58)
    c: Coincident(g62,g63)
    c: Coincident(g63,g64)
    c: Coincident(g64,g65)
    c: Coincident(g65,g62)
    c: Coincident(g66,g67)
    c: Coincident(g67,g68)
    c: Coincident(g68,g66)
    c: Coincident(g69,g70)
    c: Coincident(g70,g71)
    c: Coincident(g71,g72)
    c: Coincident(g72,g69)
    c: Coincident(g73,g74)
    c: Coincident(g74,g75)
    c: Coincident(g75,g73)
FEATURE [Part::Part2DObjectPython] Clone2D  label="Sketch (2D)"  # Draft 2D object (typed FeaturePython)
  Fuse = false
  Objects = -> [Sketch]
  Placement = pos=(-17.6,9.6,40.5) rot=(0,0,1;3.14159rad)
  Scale = (0.5,0.5,1)
FEATURE [Part::Extrusion] Extrude  label="DoubleHappinessExtruded"
  Base = -> Clone2D
  Dir = (0,0,1)
  DirMode = 2
  FaceMakerClass = Part::FaceMakerBullseye
  FaceMakerMode = 3
  LengthFwd = 1
  LengthRev = 0
  Placement = pos=(0,3.7,0.4) rot=(0,0,1;0rad)
  Solid = true
  Symmetric = false
FEATURE [Part::Fillet] Fillet006
  Base = -> Box044
  EdgeLinks = -> Box044 [Edge7,Edge12]
  Edges = 2 edges: [Edge7 r=3,Edge12 r=2]
FEATURE [Part::Fillet] Fillet007
  Base = -> Box042
  EdgeLinks = -> Box042 [Edge7]
  Edges = 1 edges r=8: [Edge7]
FEATURE [Part::Fillet] Fillet008
  Base = -> Box045
  EdgeLinks = -> Box045 [Edge12]
  Edges = 1 edges r=8: [Edge12]
FEATURE [Part::Fillet] Fillet
  Base = -> Box002
  EdgeLinks = -> Box002 [Edge12]
  Edges = 1 edges r=7: [Edge12]
FEATURE [Part::Fillet] Fillet009  label="BottomBackWallFillet"
  Base = -> Box029
  EdgeLinks = -> Box029 [Edge7]
  Edges = 1 edges r=7: [Edge7]
FEATURE [Part::Chamfer] Chamfer
  Base = -> Cylinder009
  EdgeLinks = -> Cylinder009 [Edge2]
  Edges = 1 edges: [Edge2 r1=3.9 r2=0.5]
FEATURE [Part::MultiFuse] Fusion006
  Shapes = -> [Cylinder008,Chamfer]
FEATURE [Part::Mirroring] Part__Mirroring012  label="Fusion006 (Mirror #11)"
  Base = (0,0,3)
  Normal = (0,0,1)
  Source = -> Fusion006
FEATURE [Part::Mirroring] Part__Mirroring015  label="Fusion006 (Mirror #11)001"
  Base = (1.52588e-05,-23.5,33.5)
  Normal = (1,-4e-16,-3.57628e-07)
  Source = -> Part__Mirroring012
FEATURE [Part::MultiFuse] Fusion007  label="BottomScrewHoles"
  Shapes = -> [Part__Mirroring012,Fusion006,Part__Mirroring015]
FEATURE [Part::Box] Box046  label="Cube"
  AttacherType = Attacher::AttachEngine3D
  Height = 3.01
  Length = 3.01
  Placement = pos=(-73,3,-32.5) rot=(0,0,1;0rad)
  Width = 4.01
FEATURE [Part::Chamfer] Chamfer007  label="FourthEdge"
  Base = -> Box046
  EdgeLinks = -> Box046 [Edge5,Edge7,Edge10,Edge12]
  Edges = 4 edges: [Edge5 r1=2 r2=3,Edge7 r1=2 r2=3,Edge10 r1=3 r2=2,Edge12 r1=3 r2=2]
FEATURE [Part::Mirroring] Part__Mirroring020  label="Cylinder011 (Mirror #16)"
  Base = (0,0,0)
  Normal = (1,0,0)
  Source = -> Part__Mirroring018
FEATURE [Part::Box] Box048  label="Cube037"
  AttacherType = Attacher::AttachEngine3D
  Height = 61.5
  Length = 1
  Placement = pos=(-76.3,-24.55,-37.5) rot=(0,0,1;0rad)
  Width = 31.1
FEATURE [Part::Box] Box049  label="Cube038"
  AttacherType = Attacher::AttachEngine3D
  Height = 65
  Length = 4
  Placement = pos=(-78.6,-20.7,-35) rot=(0,0,1;0rad)
  Width = 23
FEATURE [Part::Box] Box050  label="Cube039"
  AttacherType = Attacher::AttachEngine3D
  Height = 66
  Length = 1.5
  Placement = pos=(-80,-23.5,-37.5) rot=(0,0,1;0rad)
  Width = 33
FEATURE [Part::Fillet] Fillet011
  Base = -> Box050
  EdgeLinks = -> Box050 [Edge12]
  Edges = 1 edges r=7: [Edge12]
FEATURE [Part::Box] Box051  label="SpacerCoverSlider"
  AttacherType = Attacher::AttachEngine3D
  Height = 62.75
  Length = 2
  Placement = pos=(-76.8,-25.65,-37.5) rot=(0,0,1;0rad)
  Width = 33.2
FEATURE [Part::Box] Box052  label="Cube040"
  AttacherType = Attacher::AttachEngine3D
  Height = 10
  Length = 65.1
  Placement = pos=(14.9,-24,-42.9) rot=(0,0,1;0rad)
  Width = 10
FEATURE [Part::Cut] Cut042  label="BottomPlate"
  Base = -> Fusion003
  Tool = -> Box052
FEATURE [Part::Cut] Cut022  label="BottomPlateWithRPiScrewHoles"
  Base = -> Cut042
  Tool = -> Fusion004
FEATURE [Part::Cut] Cut024  label="BottomPlateWithScrewHoles"
  Base = -> Cut022
  Tool = -> Fusion007
FEATURE [Part::Box] Box055  label="Cube043"
  AttacherType = Attacher::AttachEngine3D
  Height = 3.11
  Length = 3.11
  Placement = pos=(-72.95,2.9,-32.5) rot=(0,0,1;0rad)
  Width = 4.21
FEATURE [Part::Chamfer] Chamfer008  label="FourthEdgeGap"
  Base = -> Box055
  EdgeLinks = -> Box055 [Edge5,Edge7,Edge10,Edge12]
  Edges = 4 edges: [Edge5 r1=2.1 r2=3.1,Edge7 r1=2.1 r2=3.1,Edge10 r1=3.1 r2=2.1,Edge12 r1=3.1 r2=2.1]
FEATURE [Part::Box] Box057  label="Cube045"
  AttacherType = Attacher::AttachEngine3D
  Height = 12.6
  Length = 10
  Placement = pos=(-4.8,32.3179,22.8421) rot=(1,0,0;2.35619rad)
  Width = 2
FEATURE [Part::Box] Box058  label="Cube046"
  AttacherType = Attacher::AttachEngine3D
  Height = 10
  Length = 26.7
  Placement = pos=(-13.3,12.5158,25.9508) rot=(1,0,0;0.785398rad)
  Width = 10
FEATURE [Part::Chamfer] Chamfer009
  Base = -> Box058
  EdgeLinks = -> Box058 [Edge12]
  Edges = 1 edges r=1.2: [Edge12]
FEATURE [Part::Box] Box059  label="Cube047"
  AttacherType = Attacher::AttachEngine3D
  Height = 61.5
  Length = 2.2
  Placement = pos=(-78.5,-22.4,-37.5) rot=(0,0,1;0rad)
  Width = 27.6
FEATURE [Part::Box] Box060  label="SpacerCoverOutside"
  AttacherType = Attacher::AttachEngine3D
  Height = 66
  Length = 2
  Placement = pos=(-80,-24.1,-37.5) rot=(0,0,1;0rad)
  Width = 33.6
FEATURE [Part::Cylinder] Cylinder012
  Angle = 360
  AttacherType = Attacher::AttachEngine3D
  FirstAngle = 0
  Height = 3.5
  Placement = pos=(-78.8,3.4,17.85) rot=(0,1,0;1.5708rad)
  Radius = 1.7
  SecondAngle = 0
FEATURE [Part::Cylinder] Cylinder013
  Angle = 360
  AttacherType = Attacher::AttachEngine3D
  FirstAngle = 0
  Height = 2.5
  Placement = pos=(-73.9,2.8,19.5) rot=(0,1,0;1.5708rad)
  Radius = 3.1
  SecondAngle = 0
FEATURE [Part::MultiFuse] Fusion014
  Shapes = -> [Box051,Box060,Cylinder013,Box]
FEATURE [Part::Box] Box062  label="KeepRPiConnectorFrame"
  AttacherType = Attacher::AttachEngine3D
  Height = 57
  Length = 3
  Placement = pos=(-77.5,-19.5,-33.45) rot=(0,0,1;0rad)
  Width = 21
FEATURE [Part::MultiFuse] Fusion018  label="ConnectorCoverSlider"
  Shapes = -> [Box059,Box048]
FEATURE [Part::MultiFuse] Fusion013
  Shapes = -> [Fillet011,Fusion018]
FEATURE [Part::Cut] Cut041  label="ConnectorCover"
  Base = -> Fusion013
  Tool = -> Box049
FEATURE [Part::Chamfer] Chamfer010  label="ConnectorCoverChamfered"
  Base = -> Cut041
  EdgeLinks = -> Cut041 [Edge26]
  Edges = 1 edges: [Edge26 r1=3 r2=1]
FEATURE [Part::Part2DObjectPython] Circle  # Draft 2D object (typed FeaturePython)
  Area = 0.282743
  FirstAngle = 0
  LastAngle = 0
  MakeFace = true
  Placement = pos=(-79.2977,-26.5,-37.1591) rot=(0,0.707107,0.707107;3.14159rad)
  Radius = 0.3
FEATURE [Part::FeaturePython] Array  # Draft array (typed FeaturePython)
  AlwaysSyncPlacement = false
  Angle = 360
  ArrayType = 0
  Axis = (0,0,1)
  Base = -> Circle
  Center = (0,0,0)
  Count = 15
  ExpandArray = false
  Fuse = false
  IntervalAxis = (0,0,0)
  IntervalX = (1.65,0,0)
  IntervalY = (0,20,0)
  IntervalZ = (0,0,15.2)
  NumberCircles = 3
  NumberPolar = 5
  NumberX = 3
  NumberY = 1
  NumberZ = 5
  PlacementList = 15 placements: [(-79.2977,-26.5,-37.1591),(-79.2977,-26.5,-21.9591),(-79.2977,-26.5,-6.75908),(-79.2977,-26.5,8.44092),(-79.2977,-26.5,23.6409),(-77.6477,-26.5,-37.1591),(-77.6477,-26.5,-21.9591),(-77.6477,-26.5,-6.75908),(-77.6477,-26.5,8.44092),(-77.6477,-26.5,23.6409),(-75.9977,-26.5,-37.1591),(-75.9977,-26.5,-21.9591),(-75.9977,-26.5,-6.75908),(-75.9977,-26.5,8.44092),(-75.9977,-26.5,23.6409)]
  RadialDistance = 50
  ScaleList = (15) [(1,1,1),(1,1,1),(1,1,1),(1,1,1),(1,1,1),(1,1,1),(1,1,1),(1,1,1),(1,1,1),(1,1,1),(1,1,1),(1,1,1),(1,1,1),(1,1,1),(1,1,1)]
  Symmetry = 1
  TangentialDistance = 25
FEATURE [Part::Extrusion] Extrude003  label="Nobs"
  Base = -> Array
  Dir = (2e-16,1,-2e-16)
  DirMode = 2
  FaceMakerClass = Part::FaceMakerBullseye
  FaceMakerMode = 3
  LengthFwd = 5
  LengthRev = 0
  Solid = false
  Symmetric = false
FEATURE [Part::Mirroring] Part__Mirroring021  label="Nobs (Mirror #17)"
  Base = (0,-8.9,0)
  Normal = (0,1,0)
  Source = -> Extrude003
FEATURE [Part::Box] Box064  label="Cube052"
  AttacherType = Attacher::AttachEngine3D
  Height = 3.8
  Length = 10
  Placement = pos=(-78.5,-2.7,16.15) rot=(0,0,1;0rad)
  Width = 10
FEATURE [Part::MultiFuse] Fusion019
  Shapes = -> [Box064,Cylinder012]
FEATURE [Part::Cut] Cut045  label="ConnectorCoverWithMagnet"
  Base = -> Chamfer010
  Tool = -> Fusion019
FEATURE [Part::Chamfer] Chamfer011
  Base = -> Box062
  EdgeLinks = -> Box062 [Edge1,Edge3]
  Edges = 2 edges r=2: [Edge1,Edge3]
FEATURE [Part::Cut] Cut044  label="SpacerConnectorCover"
  Base = -> Fusion014
  Tool = -> Chamfer011
FEATURE [Part::Box] Box066  label="Cube053"
  AttacherType = Attacher::AttachEngine3D
  Height = 56.5
  Length = 87
  Placement = pos=(-74.75,-19,-34.85) rot=(0,0,1;0rad)
  Width = 20
FEATURE [Part::Chamfer] Chamfer012
  Base = -> Box066
  EdgeLinks = -> Box066 [Edge3,Edge4,Edge11]
  Edges = 3 edges: [Edge3 r=3,Edge4 r=2,Edge11 r=3]
FEATURE [Part::MultiFuse] Fusion012  label="ConnectorWindows"
  Shapes = -> [Cylinder006,Box019,Box020,Cylinder010,Box030,Box012,Box010,Box011,Fillet004,Fillet005,Chamfer012]
FEATURE [Part::Cut] Cut013  label="SideWallWithPorts"
  Base = -> Fillet
  Tool = -> Fusion012
FEATURE [Part::Cut] Cut016  label="BottomBackWallWithPorts"
  Base = -> Fillet009
  Tool = -> Fusion012
FEATURE [Part::MultiFuse] Fusion005  label="BottomWithScrewHolesAndSupports"
  Shapes = -> [Part__Mirroring009,Tube,Part__Mirroring010,Part__Mirroring008,Cut016,Cut013,Cut024,Chamfer007]
FEATURE [Part::Cut] Cut039  label="PlasticPlayer3_Bottom"
  Base = -> Fusion005
  Tool = -> Cut044
FEATURE [Part::Feature] Compound
  Placement = pos=(0,0,-37.5) rot=(0,0,1;0rad)
  shape: bbox 35.81 x 22.78 x 2e-07 mm, 20 faces, 0 solids (baked)
FEATURE [Part::Extrusion] Extrude004
  Base = -> Compound
  Dir = (0,0,1)
  DirMode = 2
  FaceMakerClass = Part::FaceMakerBullseye
  FaceMakerMode = 3
  LengthFwd = 0.5
  LengthRev = 0
  Placement = pos=(0,0,-25.2) rot=(0,0,1;0rad)
  Solid = false
  Symmetric = false
FEATURE [Part::MultiFuse] Fusion010  label="Decoration"
  Shapes = -> [Extrude,Extrude004]
FEATURE [Part::Cylinder] Cylinder014
  Angle = 360
  AttacherType = Attacher::AttachEngine3D
  FirstAngle = 0
  Height = 5
  Placement = pos=(11.27,12.1446,36.8014) rot=(1,0,0;5.49779rad)
  Radius = 0.65
  SecondAngle = 0
FEATURE [Part::Mirroring] Part__Mirroring024  label="Cylinder014 (Mirror #20)"
  Base = (0,0,0)
  Normal = (1,0,0)
  Source = -> Cylinder014
FEATURE [Part::Mirroring] Part__Mirroring025  label="Cylinder014 (Mirror #21)"
  Base = (0,0,8.7)
  Normal = (0,1,-1)
  Source = -> Cylinder014
FEATURE [Part::Mirroring] Part__Mirroring026  label="Cylinder014 (Mirror #22)"
  Base = (0,0,0)
  Normal = (1,0,0)
  Source = -> Part__Mirroring025
FEATURE [Part::MultiFuse] Fusion011  label="TopBottomScrewHoles"
  Shapes = -> [Cylinder011,Part__Mirroring018,Part__Mirroring020,Cylinder014,Part__Mirroring024,Part__Mirroring025,Part__Mirroring026]
FEATURE [Part::Cylinder] Cylinder015
  Angle = 360
  AttacherType = Attacher::AttachEngine3D
  FirstAngle = 0
  Height = 1.8
  Placement = pos=(11.27,13.1814,37.8414) rot=(1,0,0;5.49779rad)
  Radius = 2
  SecondAngle = 0
FEATURE [Part::Mirroring] Part__Mirroring003  label="DisplayScrewSupport 4"
  Base = (3.8147e-06,15.3945,34.3294)
  Normal = (1,0,-1.19209e-07)
  Source = -> Cylinder015
FEATURE [Part::Mirroring] Part__Mirroring022  label="DisplayScrewSupport 3 (Mirror #18)"
  Base = (0,0,8.7)
  Normal = (0,1,-1)
  Source = -> Cylinder015
FEATURE [Part::Mirroring] Part__Mirroring023  label="DisplayScrewSupport 3 (Mirror #19)"
  Base = (0,0,0)
  Normal = (1,0,0)
  Source = -> Part__Mirroring022
FEATURE [Part::Box] Box068  label="Cube055"
  AttacherType = Attacher::AttachEngine3D
  Height = 8.6
  Length = 91
  Placement = pos=(-80,-2.7,14.9) rot=(0,0,1;0rad)
  Width = 10
FEATURE [Part::Fillet] Fillet014
  Base = -> Box068
  EdgeLinks = -> Box068 [Edge11,Edge12]
  Edges = 2 edges r=3: [Edge11,Edge12]
FEATURE [Part::MultiFuse] Fusion009  label="SpaceForBottom"
  Shapes = -> [Fillet006,Fillet007,Fillet008,Chamfer008,Fillet014]
FEATURE [Part::Part2DObjectPython] Wire  label="TopContour"  # Draft 2D object (typed FeaturePython)
  Area = 811.272
  ChamferSize = 0
  Closed = true
  End = (80,-24,-30.5)
  FilletRadius = 0
  Length = 369.594
  MakeFace = true
  Placement = pos=(80,-24,-37.5) rot=(0,0,1;0rad)
  Points = (10) [(0,0,0),(0,59,0),(0,59,60.7),(0,40.7,79),(0,-3.55271e-15,79),(0,-3.55271e-15,74),(0,40.4631,74),(0,57,57.4653),(0,57,7),(0,0,7)]
  Start = (80,-24,-37.5)
  Subdivisions = 0
FEATURE [Part::Part2DObjectPython] Wire001  label="SideContour"  # Draft 2D object (typed FeaturePython)
  Area = 4493.56
  ChamferSize = 0
  Closed = true
  End = (80,-24,41.5)
  FilletRadius = 0
  Length = 265.28
  MakeFace = true
  Placement = pos=(80,-24,-37.5) rot=(0,0,1;0rad)
  Points = (5) [(0,0,0),(0,59,0),(0,59,60.7),(0,40.7,79),(0,-3.55271e-15,79)]
  Start = (80,-24,-37.5)
  Subdivisions = 0
FEATURE [Part::Extrusion] Extrude005  label="TopVolume"
  Base = -> Wire
  Dir = (-1,0,0)
  DirMode = 0
  FaceMakerClass = Part::FaceMakerBullseye
  FaceMakerMode = 3
  LengthFwd = 160
  LengthRev = 0
  Solid = false
  Symmetric = false
FEATURE [Part::Extrusion] Extrude006  label="SideVolume"
  Base = -> Wire001
  Dir = (-1,0,0)
  DirMode = 0
  FaceMakerClass = Part::FaceMakerBullseye
  FaceMakerMode = 3
  LengthFwd = 9
  LengthRev = 0
  Solid = false
  Symmetric = false
FEATURE [Part::Mirroring] Part__Mirroring027  label="SideVolume (Mirror #23)"
  Base = (0,0,0)
  Normal = (1,0,0)
  Source = -> Extrude006
FEATURE [Part::MultiFuse] Fusion020  label="TopAndSideVolume"
  Shapes = -> [Extrude006,Part__Mirroring027,Extrude005,Chamfer004,Part__Mirroring016,Part__Mirroring017,Cut019]
FEATURE [Part::MultiFuse] Fusion021  label="TopAndSideHoles"
  Shapes = -> [Part__Mirroring001,Cylinder,Cylinder001,Box009,Fusion009,Fusion010,Box005,Box057,Chamfer009]
FEATURE [Part::Cut] Cut046  label="TopAndSideVolumeWithHoles"
  Base = -> Fusion020
  Tool = -> Fusion021
FEATURE [Part::MultiFuse] Fusion022  label="TopAndSideVolumeAddedInHoles"
  Shapes = -> [Cut046,Part__Mirroring003,Part__Mirroring022,Part__Mirroring023,Cylinder015]
FEATURE [Part::Cut] Cut047  label="TopAndSide"
  Base = -> Fusion022
  Refine = true
  Tool = -> Fusion011
FEATURE [Part::Fillet] Fillet015
  Base = -> Cut047
  EdgeLinks = -> Cut047 [Edge266,Edge267,Edge268,Edge497,Edge498,Edge499,Edge500,Edge501,Edge502,Edge504,Edge506]
  Edges = 11 edges r=2.5: [Edge266,Edge267,Edge268,Edge497,Edge498,Edge499,Edge500,Edge501,Edge502,Edge504,Edge506]
FEATURE [Part::Chamfer] Chamfer016
  Base = -> Fillet015
  EdgeLinks = -> Fillet015 [Edge414,Edge415,Edge416,Edge417,Edge545,Edge546,Edge547,Edge548]
  Edges = 8 edges: [Edge414 r=3,Edge415 r=3,Edge416 r=3,Edge417 r=3,Edge545 r=0.4,Edge546 r=0.4,Edge547 r=0.4,Edge548 r=0.4]
FEATURE [Part::Cylinder] Cylinder016
  Angle = 360
  AttacherType = Attacher::AttachEngine3D
  FirstAngle = 0
  Height = 10
  Placement = pos=(-78.8,-27.1,-36.6) rot=(1,0,0;4.71239rad)
  Radius = 0.3
  SecondAngle = 0
FEATURE [Part::Cylinder] Cylinder017
  Angle = 360
  AttacherType = Attacher::AttachEngine3D
  FirstAngle = 0
  Height = 10
  Placement = pos=(-78.8,-27.1,-29.5) rot=(1,0,0;4.71239rad)
  Radius = 0.3
  SecondAngle = 0
FEATURE [Part::Cylinder] Cylinder018
  Angle = 360
  AttacherType = Attacher::AttachEngine3D
  FirstAngle = 0
  Height = 10
  Placement = pos=(-78.8,-27.1,-14.4) rot=(1,0,0;4.71239rad)
  Radius = 0.3
  SecondAngle = 0
FEATURE [Part::Cylinder] Cylinder019
  Angle = 360
  AttacherType = Attacher::AttachEngine3D
  FirstAngle = 0
  Height = 10
  Placement = pos=(-78.8,-27.1,0.9) rot=(1,0,0;4.71239rad)
  Radius = 0.3
  SecondAngle = 0
FEATURE [Part::Cylinder] Cylinder020
  Angle = 360
  AttacherType = Attacher::AttachEngine3D
  FirstAngle = 0
  Height = 10
  Placement = pos=(-78.8,-27.1,16.6) rot=(1,0,0;4.71239rad)
  Radius = 0.3
  SecondAngle = 0
FEATURE [Part::Cylinder] Cylinder021
  Angle = 360
  AttacherType = Attacher::AttachEngine3D
  FirstAngle = 0
  Height = 10
  Placement = pos=(-78.8,-27.1,28.1) rot=(1,0,0;4.71239rad)
  Radius = 0.3
  SecondAngle = 0
FEATURE [Part::MultiFuse] Fusion015  label="PlasticPlayer3_BottomWithCover"
  Refine = true
  Shapes = -> [Cut039,Part__Mirroring021,Extrude003,Cut045,Cylinder016,Cylinder017,Cylinder018,Cylinder019,Cylinder020,Cylinder021]
FEATURE [Part::Fillet] Fillet016
  Base = -> Fusion015
  EdgeLinks = -> Fusion015 [Edge5,Edge7,Edge9,Edge13,Edge294]
  Edges = 5 edges r=2.5: [Edge5,Edge7,Edge9,Edge13,Edge294]
